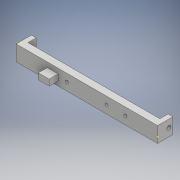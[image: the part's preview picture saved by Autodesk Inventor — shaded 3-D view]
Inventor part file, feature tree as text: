
AUTODESK INVENTOR PART (.ipt)
format: ipt  version: 2018 (Build 220112000, 112)  size: 230,912 bytes
history: native  units: mm
features: sketch x14, extrude x12, fillet x3
ambient origin geometry x8: Origin, YZ Plane, XZ Plane, XY Plane, X Axis, Y Axis, Z Axis, Center Point
bodies: Solid1 (feature_tree)
feature tree (29):
  extrude  "Extrusion1"  Depth=19.925mm
  extrude  "Extrusion2"  Depth=5.0mm
  extrude  "Extrusion3"  Depth=12.175mm TaperAngle=0.0deg
  extrude  "Extrusion4"  Depth=4.65mm TaperAngle=0.0deg
  sketch  "Sketch5"  dims[d11=10.5mm d12=2.75mm]
  extrude  "Extrusion5"  Depth=2.75mm
  extrude  "Extrusion6"  Depth=3.5mm
  extrude  "Extrusion7"  Depth=4.5mm
  fillet  "Fillet1"  Radius=5.0mm
  fillet  "Fillet2"  Radius=3.8mm
  extrude  "Extrusion8"  Depth=3.0mm
  extrude  "Extrusion9"  Depth=3.3mm
  fillet  "Fillet3"  Radius=21.0mm
  extrude  "Extrusion10"  Depth=4.0mm TaperAngle=0.0deg
  sketch  "Sketch12"  dims[d36=3.3mm d37=4.0mm d38=0.0mm]
  sketch  "Sketch13"  dims[d39=3.3mm d40=4.0mm d41=0.0mm]
  extrude  "Extrusion11"  Depth=4.0mm TaperAngle=0.0deg
  extrude  "Extrusion12"  Depth=9.5mm
  sketch  "Sketch1"  dims[d0=150.0mm d1=19.925mm]
  sketch  "Sketch2"  dims[d2=4.0mm d3=0.0mm d4=5.0mm]
  sketch  "Sketch3"  dims[d5=5.0mm d6=12.175mm d7=0.0mm]
  sketch  "Sketch4"  dims[d8=3.2mm d9=4.65mm d10=0.0mm]
  sketch  "Sketch6"  dims[d13=3.5mm d14=0.0mm d15=7.95mm]
  sketch  "Sketch7"  dims[d16=7.95mm d17=4.5mm]
  sketch  "Sketch8"  dims[d18=155.75mm d19=5.75mm d20=0.0mm d21=0.0mm]
  sketch  "Sketch9"  dims[d22=21.0mm d23=34.875mm d24=0.0mm d25=0.0mm d26=5.0mm d27=3.8mm d28=0.0mm]
  sketch  "Sketch10"  dims[d29=3.0mm d30=3.0mm]
  sketch  "Sketch11"  dims[d33=21.0mm d34=3.3mm d35=21.0mm]
  sketch  "Sketch14"  dims[d42=2.0mm d43=9.5mm d44=5.0mm d45=11.5mm d46=9.5mm d47=0.0mm d48=4.0mm d49=1.5mm d50=0.0mm d51=1.825mm d52=0.0mm]
